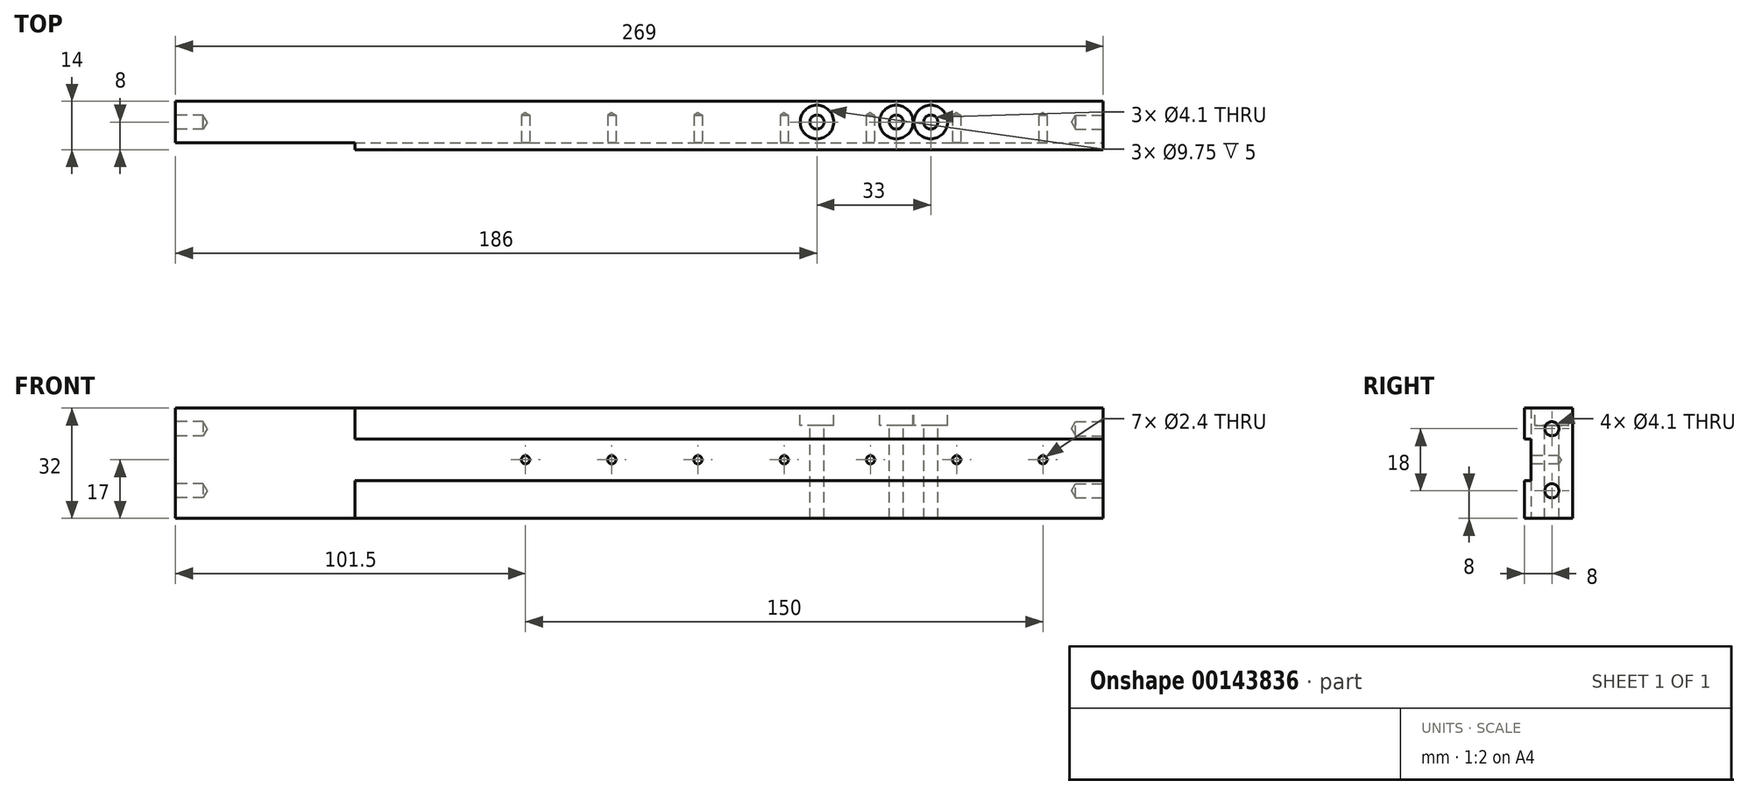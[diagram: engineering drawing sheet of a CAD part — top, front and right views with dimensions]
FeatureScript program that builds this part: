
annotation { "Feature Type Name" : "Feature", "Feature Type Description" : "" }
export const myFeature = defineFeature(function(context is Context, id is Id, definition is map)
    precondition{}
    {
        {
            var Q0;
            Q0=qCreatedBy(makeId("Front.planeOp"),FACE);
            var sketch = newSketch(context, id + "F0", { "sketchPlane" : qUnion([Q0])});
            skLineSegment(sketch, "E0.bottom", {"start": v(134.5, -16) * mm, "end": v(-134.5, -16) * mm});
            skLineSegment(sketch, "E0.top", {"start": v(134.5, 16) * mm, "end": v(-134.5, 16) * mm});
            skLineSegment(sketch, "E0.left", {"start": v(134.5, -16) * mm, "end": v(134.5, 16) * mm});
            skLineSegment(sketch, "E0.right", {"start": v(-134.5, -16) * mm, "end": v(-134.5, 16) * mm});
            skPoint(sketch, "E0.middle", {"position": v(0, 0) * mm});
            skSolve(sketch);
        }
        {
            var Q0;
            Q0=makeQuery(id+"F0.imprint","IMPRINT",FACE,{"disambiguationData":[TD([[makeQuery(id+"F0.imprint","IMPRINT",EDGE,{"derivedFrom":sQuery(id+"F0.wireOp",EDGE,"E0.bottom")}),-1.0]])]});
            extrude(context, id + "F1", {"entities" : qUnion([Q0]), "depth" : 12 * mm});
        }
        {
            var Q0;
            Q0=makeQuery(id+"F1.opExtrude","CAP_FACE",FACE,{"disambiguationData":[OSD([sQuery(id+"F0.wireOp",EDGE,"E0.bottom"),sQuery(id+"F0.wireOp",EDGE,"E0.top"),sQuery(id+"F0.wireOp",EDGE,"E0.left"),sQuery(id+"F0.wireOp",EDGE,"E0.right")])],"isStart":false});
            var sketch = newSketch(context, id + "F2", { "sketchPlane" : qUnion([Q0])});
            skLineSegment(sketch, "E1", {"start": v(-82.5, 16) * mm, "end": v(-82.5, -16) * mm});
            skLineSegment(sketch, "E2", {"start": v(-82.5, 7) * mm, "end": v(134.5, 7) * mm});
            skLineSegment(sketch, "E3", {"start": v(134.5, -5) * mm, "end": v(-82.5, -5) * mm});
            skSolve(sketch);
        }
        {
            var Q0;
            {var subQ3=sQuery(id+"F2.wireOp",EDGE,"E2");Q0=makeQuery(id+"F2.imprint","IMPRINT",FACE,{"disambiguationData":[TD([[makeQuery(id+"F2.imprint","IMPRINT",EDGE,{"derivedFrom":subQ3}),1.0]])]});}
            var Q1;
            {var subQ3=sQuery(id+"F2.wireOp",EDGE,"E3");Q1=makeQuery(id+"F2.imprint","IMPRINT",FACE,{"disambiguationData":[TD([[makeQuery(id+"F2.imprint","IMPRINT",EDGE,{"derivedFrom":subQ3}),1.0]])]});}
            extrude(context, id + "F3", {"entities" : qUnion([Q0, Q1]), "operationType" : NewBodyOperationType.ADD, "depth" : 2 * mm});
        }
        {
            var Q0;
            Q0=makeQuery(id+"F1.opExtrude","CAP_FACE",FACE,{"disambiguationData":[OSD([sQuery(id+"F0.wireOp",EDGE,"E0.bottom"),sQuery(id+"F0.wireOp",EDGE,"E0.top"),sQuery(id+"F0.wireOp",EDGE,"E0.left"),sQuery(id+"F0.wireOp",EDGE,"E0.right")])],"isStart":false});
            var sketch = newSketch(context, id + "F4", { "sketchPlane" : qUnion([Q0])});
            skCircle(sketch, "E4", {"center": v(117, 1) * mm, "radius": 2.33 * mm});
            skCircle(sketch, "E5", {"center": v(92, 1) * mm, "radius": 2.8 * mm});
            skCircle(sketch, "E6", {"center": v(67, 1) * mm, "radius": 2.4 * mm});
            skCircle(sketch, "E7", {"center": v(42, 1) * mm, "radius": 1.84 * mm});
            skCircle(sketch, "E8", {"center": v(17, 1) * mm, "radius": 2.55 * mm});
            skCircle(sketch, "E9", {"center": v(-8, 1) * mm, "radius": 2.16 * mm});
            skCircle(sketch, "E10", {"center": v(-33, 1) * mm, "radius": 2.33 * mm});
            skSolve(sketch);
        }
        {
            var Q0;
            Q0=sQuery(id+"F4.wireOp",VERTEX,"E10.center");
            var Q1;
            Q1=sQuery(id+"F4.wireOp",VERTEX,"E9.center");
            var Q2;
            Q2=sQuery(id+"F4.wireOp",VERTEX,"E8.center");
            var Q3;
            Q3=sQuery(id+"F4.wireOp",VERTEX,"E7.center");
            var Q4;
            Q4=sQuery(id+"F4.wireOp",VERTEX,"E6.center");
            var Q5;
            Q5=sQuery(id+"F4.wireOp",VERTEX,"E5.center");
            var Q6;
            Q6=sQuery(id+"F4.wireOp",VERTEX,"E4.center");
            var Q7;
            Q7=makeQuery(id+"F1.opExtrude","SWEPT_BODY",BODY,{"disambiguationData":[OSD([sQuery(id+"F0.wireOp",EDGE,"E0.bottom"),sQuery(id+"F0.wireOp",EDGE,"E0.top"),sQuery(id+"F0.wireOp",EDGE,"E0.left"),sQuery(id+"F0.wireOp",EDGE,"E0.right")])]});
            hole(context, id + "F5", {"style" : HoleStyle.SIMPLE, "endStyle" : HoleEndStyle.BLIND, "standardTappedOrClearance" : lookupTablePath({ "standard" : "ISO", "engagement" : "75%", "pitch" : "0.6 mm", "size" : "M3", "type" : "Tapped" }), "standardBlindInLast" : lookupTablePath({ "standard" : "ISO", "engagement" : "75%", "pitch" : "0.6 mm", "size" : "M3", "type" : "Tapped" }), "holeDiameter" : 2.4 * mm, "holeDepth" : 8 * mm, "startFromSketch" : true, "locations" : qUnion([Q0, Q1, Q2, Q3, Q4, Q5, Q6]), "scope" : qUnion([Q7])});
        }
        {
            var Q0;
            {var subQ0=sQuery(id+"F0.wireOp",EDGE,"E0.left");var subQ1=makeQuery(id+"F1.opExtrude","CAP_EDGE",EDGE,{"disambiguationData":[OSD([subQ0])],"isStart":false});Q0=makeQuery(id+"F3.boolean.opBoolean","MERGE",FACE,{"derivedFrom":[makeQuery(id+"F1.opExtrude","SWEPT_FACE",FACE,{"disambiguationData":[OSD([subQ0])]}),makeQuery(id+"F3.opExtrude","SWEPT_FACE",FACE,{"disambiguationData":[OSD([subQ0]),TDD([makeQuery(id+"F2.imprint","IMPRINT",EDGE,{"disambiguationData":[TD([[makeQuery(id+"F2.imprint","INTERSECT",VERTEX,{"derivedFrom":[makeQuery(id+"F1.opExtrude","CAP_EDGE",EDGE,{"disambiguationData":[OSD([sQuery(id+"F0.wireOp",EDGE,"E0.bottom")])],"isStart":false}),subQ1]}),-1.0]])],"derivedFrom":subQ1})])]}),makeQuery(id+"F3.opExtrude","SWEPT_FACE",FACE,{"disambiguationData":[OSD([subQ0]),TDD([makeQuery(id+"F2.imprint","IMPRINT",EDGE,{"disambiguationData":[TD([[makeQuery(id+"F2.imprint","INTERSECT",VERTEX,{"derivedFrom":[makeQuery(id+"F1.opExtrude","CAP_EDGE",EDGE,{"disambiguationData":[OSD([sQuery(id+"F0.wireOp",EDGE,"E0.top")])],"isStart":false}),subQ1]}),1.0]])],"derivedFrom":subQ1})])]})]});}
            var sketch = newSketch(context, id + "F6", { "sketchPlane" : qUnion([Q0])});
            skCircle(sketch, "E11", {"center": v(-6, 10) * mm, "radius": 1.82 * mm});
            skCircle(sketch, "E12", {"center": v(-6, -8) * mm, "radius": 1.8 * mm});
            skSolve(sketch);
        }
        {
            var Q0;
            Q0=sQuery(id+"F6.wireOp",VERTEX,"E11.center");
            var Q1;
            Q1=sQuery(id+"F6.wireOp",VERTEX,"E12.center");
            var Q2;
            Q2=makeQuery(id+"F1.opExtrude","SWEPT_BODY",BODY,{"disambiguationData":[OSD([sQuery(id+"F0.wireOp",EDGE,"E0.bottom"),sQuery(id+"F0.wireOp",EDGE,"E0.top"),sQuery(id+"F0.wireOp",EDGE,"E0.left"),sQuery(id+"F0.wireOp",EDGE,"E0.right")])]});
            hole(context, id + "F7", {"style" : HoleStyle.SIMPLE, "endStyle" : HoleEndStyle.BLIND, "standardTappedOrClearance" : lookupTablePath({ "standard" : "ISO", "engagement" : "75%", "pitch" : "0.9 mm", "size" : "M5", "type" : "Tapped" }), "standardBlindInLast" : lookupTablePath({ "standard" : "ISO", "engagement" : "75%", "pitch" : "0.9 mm", "size" : "M5", "type" : "Tapped" }), "holeDiameter" : 4.1 * mm, "holeDepth" : 8 * mm, "startFromSketch" : true, "locations" : qUnion([Q0, Q1]), "scope" : qUnion([Q2])});
        }
        {
            var Q0;
            Q0=makeQuery(id+"F1.opExtrude","SWEPT_FACE",FACE,{"disambiguationData":[OSD([sQuery(id+"F0.wireOp",EDGE,"E0.right")])]});
            var sketch = newSketch(context, id + "F8", { "sketchPlane" : qUnion([Q0])});
            skCircle(sketch, "E13", {"center": v(6, 10) * mm, "radius": 3.1 * mm});
            skCircle(sketch, "E14", {"center": v(6, -8) * mm, "radius": 3.36 * mm});
            skSolve(sketch);
        }
        {
            var Q0;
            Q0=sQuery(id+"F8.wireOp",VERTEX,"E13.center");
            var Q1;
            Q1=sQuery(id+"F8.wireOp",VERTEX,"E14.center");
            var Q2;
            Q2=makeQuery(id+"F1.opExtrude","SWEPT_BODY",BODY,{"disambiguationData":[OSD([sQuery(id+"F0.wireOp",EDGE,"E0.bottom"),sQuery(id+"F0.wireOp",EDGE,"E0.top"),sQuery(id+"F0.wireOp",EDGE,"E0.left"),sQuery(id+"F0.wireOp",EDGE,"E0.right")])]});
            hole(context, id + "F9", {"style" : HoleStyle.SIMPLE, "endStyle" : HoleEndStyle.BLIND, "standardTappedOrClearance" : lookupTablePath({ "standard" : "ISO", "engagement" : "75%", "pitch" : "0.9 mm", "size" : "M5", "type" : "Tapped" }), "standardBlindInLast" : lookupTablePath({ "standard" : "ISO", "engagement" : "75%", "pitch" : "0.9 mm", "size" : "M5", "type" : "Tapped" }), "holeDiameter" : 4.1 * mm, "holeDepth" : 8 * mm, "startFromSketch" : true, "locations" : qUnion([Q0, Q1]), "scope" : qUnion([Q2])});
        }
        {
            var Q0;
            {var subQ0=sQuery(id+"F0.wireOp",EDGE,"E0.top");Q0=makeQuery(id+"F3.boolean.opBoolean","MERGE",FACE,{"derivedFrom":[makeQuery(id+"F1.opExtrude","SWEPT_FACE",FACE,{"disambiguationData":[OSD([subQ0])]}),makeQuery(id+"F3.opExtrude","SWEPT_FACE",FACE,{"disambiguationData":[OSD([subQ0])]})]});}
            var sketch = newSketch(context, id + "F10", { "sketchPlane" : qUnion([Q0])});
            skCircle(sketch, "E15", {"center": v(84.5, -6) * mm, "radius": 3.7 * mm});
            skCircle(sketch, "E16", {"center": v(74.5, -6) * mm, "radius": 4.2 * mm});
            skCircle(sketch, "E17", {"center": v(51.5, -6) * mm, "radius": 2.53 * mm});
            skSolve(sketch);
        }
        {
            var Q0;
            Q0=sQuery(id+"F10.wireOp",VERTEX,"E17.center");
            var Q1;
            Q1=sQuery(id+"F10.wireOp",VERTEX,"E16.center");
            var Q2;
            Q2=sQuery(id+"F10.wireOp",VERTEX,"E15.center");
            var Q3;
            Q3=makeQuery(id+"F1.opExtrude","SWEPT_BODY",BODY,{"disambiguationData":[OSD([sQuery(id+"F0.wireOp",EDGE,"E0.bottom"),sQuery(id+"F0.wireOp",EDGE,"E0.top"),sQuery(id+"F0.wireOp",EDGE,"E0.left"),sQuery(id+"F0.wireOp",EDGE,"E0.right")])]});
            hole(context, id + "F11", {"style" : HoleStyle.C_BORE, "endStyle" : HoleEndStyle.THROUGH, "standardTappedOrClearance" : lookupTablePath({ "standard" : "ISO", "engagement" : "75%", "pitch" : "0.9 mm", "size" : "M5", "type" : "Tapped" }), "standardBlindInLast" : lookupTablePath({ "standard" : "ISO", "engagement" : "75%", "pitch" : "0.9 mm", "size" : "M5", "type" : "Tapped" }), "holeDiameter" : 4.1 * mm, "cBoreDiameter" : 9.75 * mm, "cBoreDepth" : 5 * mm, "startFromSketch" : true, "locations" : qUnion([Q0, Q1, Q2]), "scope" : qUnion([Q3]), "isTappedThrough" : true, "showTappedDepth" : true});
        }
    });
